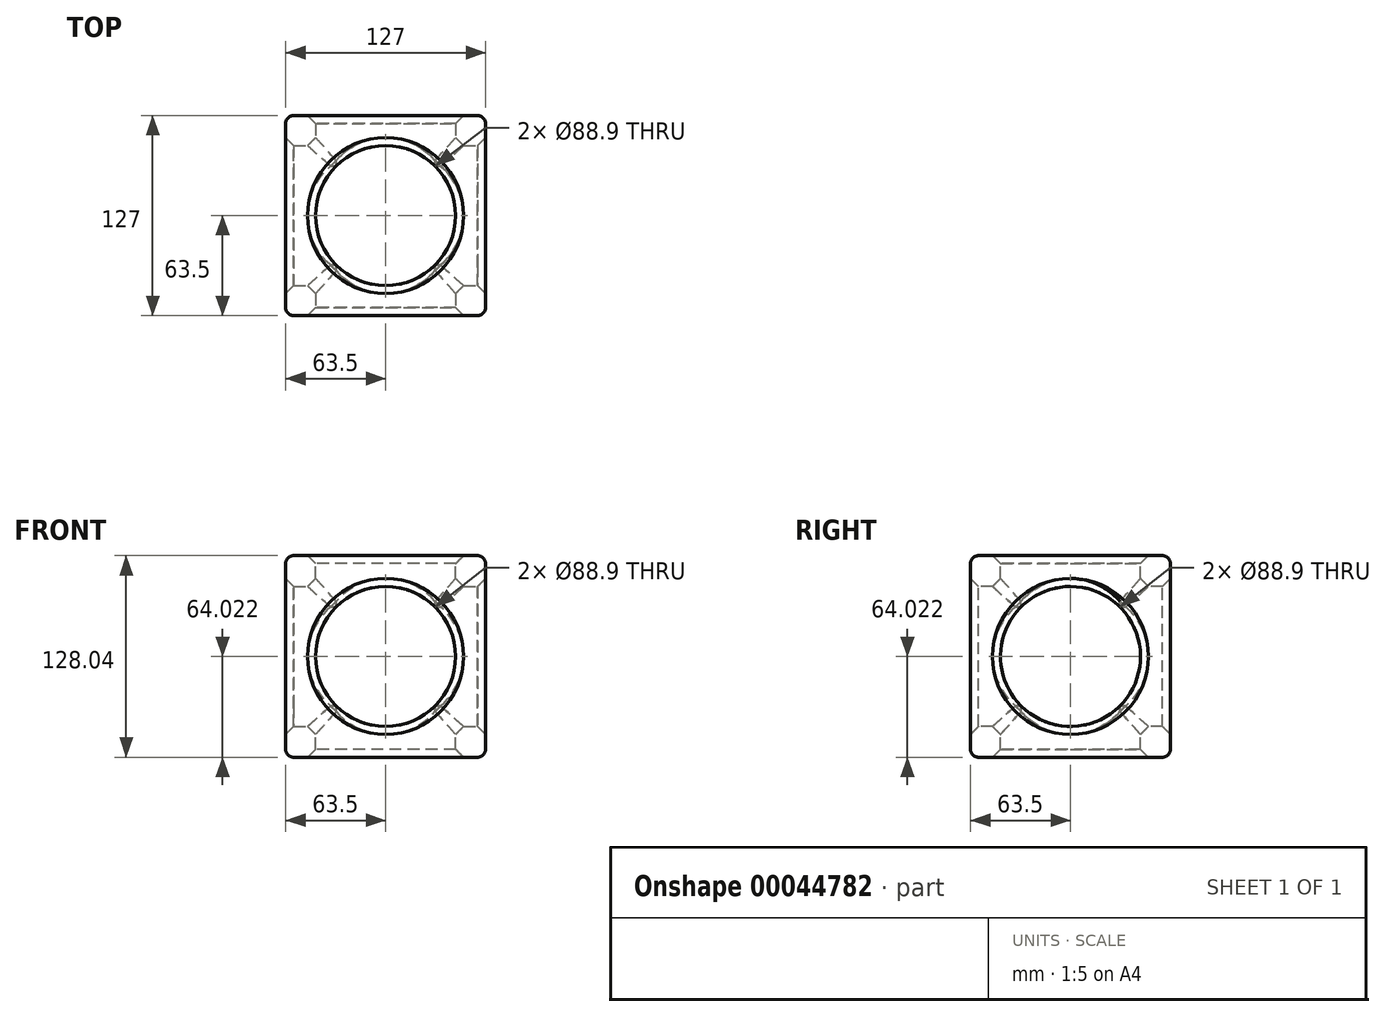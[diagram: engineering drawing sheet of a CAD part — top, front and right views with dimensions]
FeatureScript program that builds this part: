
annotation { "Feature Type Name" : "Feature", "Feature Type Description" : "" }
export const myFeature = defineFeature(function(context is Context, id is Id, definition is map)
    precondition{}
    {
        {
            var Q0;
            Q0=qCreatedBy(makeId("Front.planeOp"),FACE);
            var sketch = newSketch(context, id + "F0", { "sketchPlane" : qUnion([Q0])});
            skLineSegment(sketch, "E0.bottom", {"start": v(0, 0) * mm, "end": v(127, 0) * mm});
            skLineSegment(sketch, "E0.top", {"start": v(0, 128.04) * mm, "end": v(127, 128.04) * mm});
            skLineSegment(sketch, "E0.left", {"start": v(0, 0) * mm, "end": v(0, 128.04) * mm});
            skLineSegment(sketch, "E0.right", {"start": v(127, 0) * mm, "end": v(127, 128.04) * mm});
            skSolve(sketch);
        }
        {
            var Q0;
            Q0 = qSketchRegion(id + "F0", true);
            extrude(context, id + "F1", {"entities" : qUnion([Q0]), "depth" : 127 * mm});
        }
        {
            var Q0;
            Q0=makeQuery(id+"F1.opExtrude","SWEPT_FACE",FACE,{"disambiguationData":[OSD([sQuery(id+"F0.wireOp",EDGE,"E0.top")])]});
            var Q1;
            Q1=makeQuery(id+"F1.opExtrude","CAP_FACE",FACE,{"disambiguationData":[OSD([sQuery(id+"F0.wireOp",EDGE,"E0.bottom"),sQuery(id+"F0.wireOp",EDGE,"E0.top"),sQuery(id+"F0.wireOp",EDGE,"E0.left"),sQuery(id+"F0.wireOp",EDGE,"E0.right")])],"isStart":false});
            var Q2;
            Q2=makeQuery(id+"F1.opExtrude","SWEPT_FACE",FACE,{"disambiguationData":[OSD([sQuery(id+"F0.wireOp",EDGE,"E0.left")])]});
            var Q3;
            Q3=makeQuery(id+"F1.opExtrude","SWEPT_FACE",FACE,{"disambiguationData":[OSD([sQuery(id+"F0.wireOp",EDGE,"E0.bottom")])]});
            var Q4;
            Q4=makeQuery(id+"F1.opExtrude","CAP_FACE",FACE,{"disambiguationData":[OSD([sQuery(id+"F0.wireOp",EDGE,"E0.bottom"),sQuery(id+"F0.wireOp",EDGE,"E0.top"),sQuery(id+"F0.wireOp",EDGE,"E0.left"),sQuery(id+"F0.wireOp",EDGE,"E0.right")])],"isStart":true});
            fillet(context, id + "F2", {"entities" : qUnion([Q0, Q1, Q2, Q3, Q4]), "radius" : 5.08 * mm, "tangentPropagation" : true, "allowEdgeOverflow" : false});
        }
        {
            var Q0;
            Q0=makeQuery(id+"F1.opExtrude","CAP_FACE",FACE,{"disambiguationData":[OSD([sQuery(id+"F0.wireOp",EDGE,"E0.bottom"),sQuery(id+"F0.wireOp",EDGE,"E0.top"),sQuery(id+"F0.wireOp",EDGE,"E0.left"),sQuery(id+"F0.wireOp",EDGE,"E0.right")])],"isStart":false});
            var sketch = newSketch(context, id + "F3", { "sketchPlane" : qUnion([Q0])});
            skLineSegment(sketch, "E1", {"start": v(121.92, 122.96) * mm, "end": v(5.08, 5.08) * mm});
            skLineSegment(sketch, "E2", {"start": v(121.92, 5.08) * mm, "end": v(5.08, 122.96) * mm});
            skCircle(sketch, "E3", {"center": v(63.5, 64.02) * mm, "radius": 44.45 * mm});
            skSolve(sketch);
        }
        {
            var Q0;
            {var subQ0=sQuery(id+"F3.wireOp",EDGE,"E3");var subQ3=sQuery(id+"F3.wireOp",EDGE,"E1");var subQ4=makeQuery(id+"F3.imprint","INTERSECT",VERTEX,{"disambiguationData":[OD(0.0)],"derivedFrom":[subQ3,subQ0]});Q0=makeQuery(id+"F3.imprint","IMPRINT",FACE,{"disambiguationData":[TD([[makeQuery(id+"F3.imprint","IMPRINT",EDGE,{"disambiguationData":[TD([[subQ4,-1.0]])],"derivedFrom":subQ3}),1.0]])]});}
            var Q1;
            {var subQ0=sQuery(id+"F3.wireOp",EDGE,"E3");var subQ3=sQuery(id+"F3.wireOp",EDGE,"E1");var subQ4=makeQuery(id+"F3.imprint","INTERSECT",VERTEX,{"disambiguationData":[OD(0.0)],"derivedFrom":[subQ3,subQ0]});Q1=makeQuery(id+"F3.imprint","IMPRINT",FACE,{"disambiguationData":[TD([[makeQuery(id+"F3.imprint","IMPRINT",EDGE,{"disambiguationData":[TD([[subQ4,-1.0]])],"derivedFrom":subQ3}),-1.0]])]});}
            var Q2;
            {var subQ1=sQuery(id+"F3.wireOp",EDGE,"E2");var subQ3=sQuery(id+"F3.wireOp",EDGE,"E1");var subQ5=makeQuery(id+"F3.imprint","INTERSECT",VERTEX,{"derivedFrom":[subQ3,subQ1]});Q2=makeQuery(id+"F3.imprint","IMPRINT",FACE,{"disambiguationData":[TD([[makeQuery(id+"F3.imprint","IMPRINT",EDGE,{"disambiguationData":[TD([[subQ5,-1.0]])],"derivedFrom":subQ3}),1.0]])]});}
            var Q3;
            {var subQ1=sQuery(id+"F3.wireOp",EDGE,"E2");var subQ3=sQuery(id+"F3.wireOp",EDGE,"E1");var subQ5=makeQuery(id+"F3.imprint","INTERSECT",VERTEX,{"derivedFrom":[subQ3,subQ1]});Q3=makeQuery(id+"F3.imprint","IMPRINT",FACE,{"disambiguationData":[TD([[makeQuery(id+"F3.imprint","IMPRINT",EDGE,{"disambiguationData":[TD([[subQ5,-1.0]])],"derivedFrom":subQ3}),-1.0]])]});}
            extrude(context, id + "F4", {"entities" : qUnion([Q0, Q1, Q2, Q3]), "operationType" : NewBodyOperationType.REMOVE, "endBound" : BoundingType.THROUGH_ALL, "oppositeDirection" : true, "depth" : 127 * mm});
        }
        {
            var Q0;
            Q0=makeQuery(id+"F1.opExtrude","SWEPT_FACE",FACE,{"disambiguationData":[OSD([sQuery(id+"F0.wireOp",EDGE,"E0.right")])]});
            var sketch = newSketch(context, id + "F5", { "sketchPlane" : qUnion([Q0])});
            skLineSegment(sketch, "E4", {"start": v(-5.08, 5.08) * mm, "end": v(-121.92, 122.96) * mm});
            skLineSegment(sketch, "E5", {"start": v(-121.92, 5.08) * mm, "end": v(-5.08, 122.96) * mm});
            skCircle(sketch, "E6", {"center": v(-63.5, 64.02) * mm, "radius": 44.45 * mm});
            skSolve(sketch);
        }
        {
            var Q0;
            {var subQ0=sQuery(id+"F5.wireOp",EDGE,"E6");var subQ3=sQuery(id+"F5.wireOp",EDGE,"E4");var subQ4=makeQuery(id+"F5.imprint","INTERSECT",VERTEX,{"disambiguationData":[OD(0.0)],"derivedFrom":[subQ3,subQ0]});Q0=makeQuery(id+"F5.imprint","IMPRINT",FACE,{"disambiguationData":[TD([[makeQuery(id+"F5.imprint","IMPRINT",EDGE,{"disambiguationData":[TD([[subQ4,-1.0]])],"derivedFrom":subQ3}),1.0]])]});}
            var Q1;
            {var subQ1=sQuery(id+"F5.wireOp",EDGE,"E6");var subQ3=sQuery(id+"F5.wireOp",EDGE,"E4");var subQ5=makeQuery(id+"F5.imprint","INTERSECT",VERTEX,{"disambiguationData":[OD(0.0)],"derivedFrom":[subQ3,subQ1]});Q1=makeQuery(id+"F5.imprint","IMPRINT",FACE,{"disambiguationData":[TD([[makeQuery(id+"F5.imprint","IMPRINT",EDGE,{"disambiguationData":[TD([[subQ5,-1.0]])],"derivedFrom":subQ3}),-1.0]])]});}
            var Q2;
            {var subQ1=sQuery(id+"F5.wireOp",EDGE,"E5");var subQ3=sQuery(id+"F5.wireOp",EDGE,"E4");var subQ5=makeQuery(id+"F5.imprint","INTERSECT",VERTEX,{"derivedFrom":[subQ3,subQ1]});Q2=makeQuery(id+"F5.imprint","IMPRINT",FACE,{"disambiguationData":[TD([[makeQuery(id+"F5.imprint","IMPRINT",EDGE,{"disambiguationData":[TD([[subQ5,-1.0]])],"derivedFrom":subQ3}),1.0]])]});}
            var Q3;
            {var subQ1=sQuery(id+"F5.wireOp",EDGE,"E5");var subQ3=sQuery(id+"F5.wireOp",EDGE,"E4");var subQ5=makeQuery(id+"F5.imprint","INTERSECT",VERTEX,{"derivedFrom":[subQ3,subQ1]});Q3=makeQuery(id+"F5.imprint","IMPRINT",FACE,{"disambiguationData":[TD([[makeQuery(id+"F5.imprint","IMPRINT",EDGE,{"disambiguationData":[TD([[subQ5,-1.0]])],"derivedFrom":subQ3}),-1.0]])]});}
            extrude(context, id + "F6", {"entities" : qUnion([Q0, Q1, Q2, Q3]), "operationType" : NewBodyOperationType.REMOVE, "endBound" : BoundingType.THROUGH_ALL, "oppositeDirection" : true, "depth" : 127 * mm});
        }
        {
            var Q0;
            Q0=makeQuery(id+"F1.opExtrude","SWEPT_FACE",FACE,{"disambiguationData":[OSD([sQuery(id+"F0.wireOp",EDGE,"E0.top")])]});
            var sketch = newSketch(context, id + "F7", { "sketchPlane" : qUnion([Q0])});
            skLineSegment(sketch, "E7", {"start": v(5.08, -121.92) * mm, "end": v(121.92, -5.08) * mm});
            skLineSegment(sketch, "E8", {"start": v(5.08, -5.08) * mm, "end": v(121.92, -121.92) * mm});
            skCircle(sketch, "E9", {"center": v(63.5, -63.5) * mm, "radius": 44.45 * mm});
            skSolve(sketch);
        }
        {
            var Q0;
            Q0 = qSketchRegion(id + "F7", true);
            extrude(context, id + "F8", {"entities" : qUnion([Q0]), "operationType" : NewBodyOperationType.REMOVE, "endBound" : BoundingType.THROUGH_ALL, "oppositeDirection" : true, "depth" : 127 * mm});
        }
        {
            var Q0;
            {var subQ0=makeQuery(id+"F6.opExtrude","SWEPT_FACE",FACE,{"disambiguationData":[OSD([sQuery(id+"F5.wireOp",EDGE,"E6")])]});Q0=makeQuery(id+"F6.boolean.opBoolean","COPY",FACE,{"disambiguationData":[TD([makeQuery(id+"F1.opExtrude","SWEPT_FACE",FACE,{"disambiguationData":[OSD([sQuery(id+"F0.wireOp",EDGE,"E0.left")])]})])],"derivedFrom":subQ0});}
            var Q1;
            Q1=makeQuery(id+"F8.boolean.opBoolean","COPY",FACE,{"disambiguationData":[TD([makeQuery(id+"F1.opExtrude","SWEPT_FACE",FACE,{"disambiguationData":[OSD([sQuery(id+"F0.wireOp",EDGE,"E0.bottom")])]})])],"derivedFrom":makeQuery(id+"F8.opExtrude","SWEPT_FACE",FACE,{"disambiguationData":[OSD([sQuery(id+"F7.wireOp",EDGE,"E9")])]})});
            var Q2;
            {var subQ0=makeQuery(id+"F4.boolean.opBoolean","COPY",FACE,{"derivedFrom":makeQuery(id+"F4.opExtrude","SWEPT_FACE",FACE,{"disambiguationData":[OSD([sQuery(id+"F3.wireOp",EDGE,"E3")])]})});Q2=makeQuery(id+"F6.boolean.opBoolean","SPLIT",FACE,{"disambiguationData":[TD([makeQuery(id+"F1.opExtrude","CAP_FACE",FACE,{"disambiguationData":[OSD([sQuery(id+"F0.wireOp",EDGE,"E0.bottom"),sQuery(id+"F0.wireOp",EDGE,"E0.top"),sQuery(id+"F0.wireOp",EDGE,"E0.left"),sQuery(id+"F0.wireOp",EDGE,"E0.right")])],"isStart":true})])],"derivedFrom":subQ0});}
            var Q3;
            {var subQ0=makeQuery(id+"F6.opExtrude","SWEPT_FACE",FACE,{"disambiguationData":[OSD([sQuery(id+"F5.wireOp",EDGE,"E6")])]});Q3=makeQuery(id+"F6.boolean.opBoolean","COPY",FACE,{"disambiguationData":[TD([makeQuery(id+"F1.opExtrude","SWEPT_FACE",FACE,{"disambiguationData":[OSD([sQuery(id+"F0.wireOp",EDGE,"E0.right")])]})])],"derivedFrom":subQ0});}
            var Q4;
            Q4=makeQuery(id+"F8.boolean.opBoolean","COPY",FACE,{"disambiguationData":[TD([makeQuery(id+"F1.opExtrude","SWEPT_FACE",FACE,{"disambiguationData":[OSD([sQuery(id+"F0.wireOp",EDGE,"E0.top")])]})])],"derivedFrom":makeQuery(id+"F8.opExtrude","SWEPT_FACE",FACE,{"disambiguationData":[OSD([sQuery(id+"F7.wireOp",EDGE,"E9")])]})});
            var Q5;
            {var subQ0=makeQuery(id+"F4.boolean.opBoolean","COPY",FACE,{"derivedFrom":makeQuery(id+"F4.opExtrude","SWEPT_FACE",FACE,{"disambiguationData":[OSD([sQuery(id+"F3.wireOp",EDGE,"E3")])]})});Q5=makeQuery(id+"F6.boolean.opBoolean","SPLIT",FACE,{"disambiguationData":[TD([makeQuery(id+"F1.opExtrude","CAP_FACE",FACE,{"disambiguationData":[OSD([sQuery(id+"F0.wireOp",EDGE,"E0.bottom"),sQuery(id+"F0.wireOp",EDGE,"E0.top"),sQuery(id+"F0.wireOp",EDGE,"E0.left"),sQuery(id+"F0.wireOp",EDGE,"E0.right")])],"isStart":false})])],"derivedFrom":subQ0});}
            chamfer(context, id + "F9", {"entities" : qUnion([Q0, Q1, Q2, Q3, Q4, Q5]), "width" : 5.08 * mm, "tangentPropagation" : true});
        }
    });
